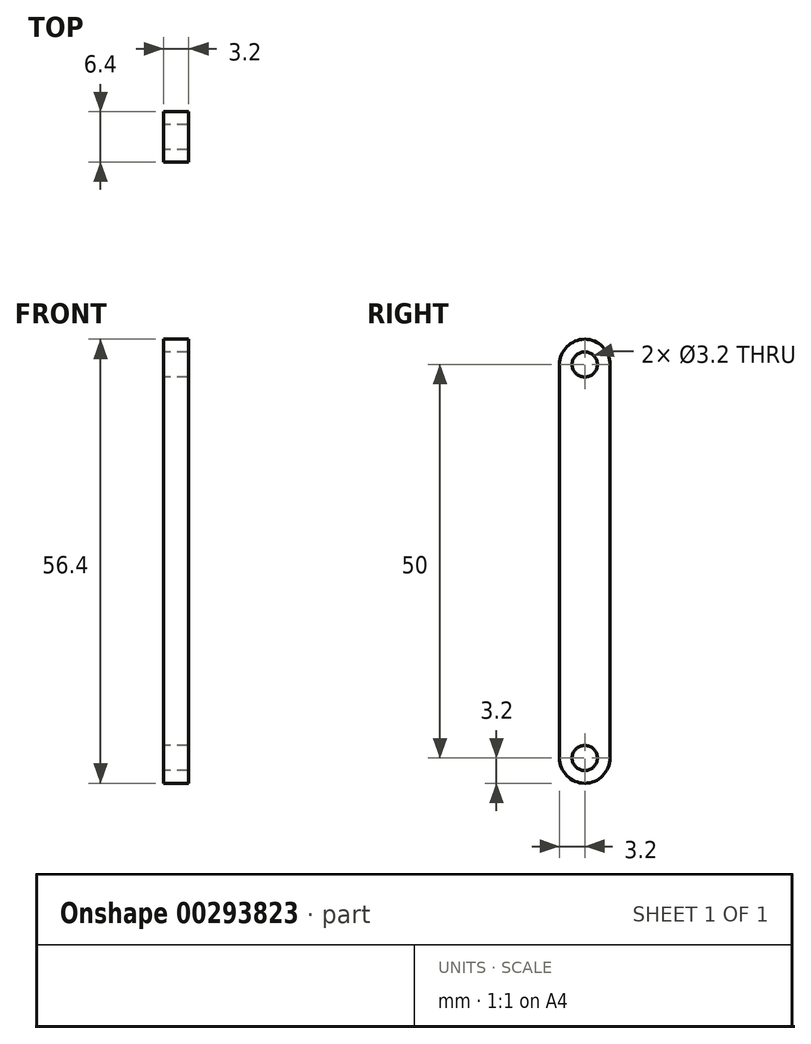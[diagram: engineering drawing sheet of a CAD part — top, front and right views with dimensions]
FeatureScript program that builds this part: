
annotation { "Feature Type Name" : "Feature", "Feature Type Description" : "" }
export const myFeature = defineFeature(function(context is Context, id is Id, definition is map)
    precondition{}
    {
        {
            var Q0;
            Q0=qCreatedBy(makeId("Right.planeOp"),FACE);
            var sketch = newSketch(context, id + "F0", { "sketchPlane" : qUnion([Q0])});
            skLineSegment(sketch, "E0", {"start": v(0, 25) * mm, "end": v(0, -25) * mm});
            skLineSegment(sketch, "E1", {"start": v(6.4, -25) * mm, "end": v(6.4, 25) * mm});
            skArc(sketch, "E2", {"start": v(6.4, 25) * mm, "mid": v(3.2, 28.2) * mm, "end": v(0, 25) * mm});
            skArc(sketch, "E3", {"start": v(0, -25) * mm, "mid": v(3.2, -28.2) * mm, "end": v(6.4, -25) * mm});
            skCircle(sketch, "E4", {"center": v(3.2, 25) * mm, "radius": 1.6 * mm});
            skCircle(sketch, "E5", {"center": v(3.2, -25) * mm, "radius": 1.6 * mm});
            skSolve(sketch);
        }
        {
            var Q0;
            Q0=makeQuery(id+"F0.imprint","IMPRINT",FACE,{"disambiguationData":[TD([[makeQuery(id+"F0.imprint","IMPRINT",EDGE,{"derivedFrom":sQuery(id+"F0.wireOp",EDGE,"E0")}),1.0]])]});
            extrude(context, id + "F1", {"entities" : qUnion([Q0]), "endBound" : BoundingType.SYMMETRIC, "depth" : 3.2 * mm});
        }
    });
